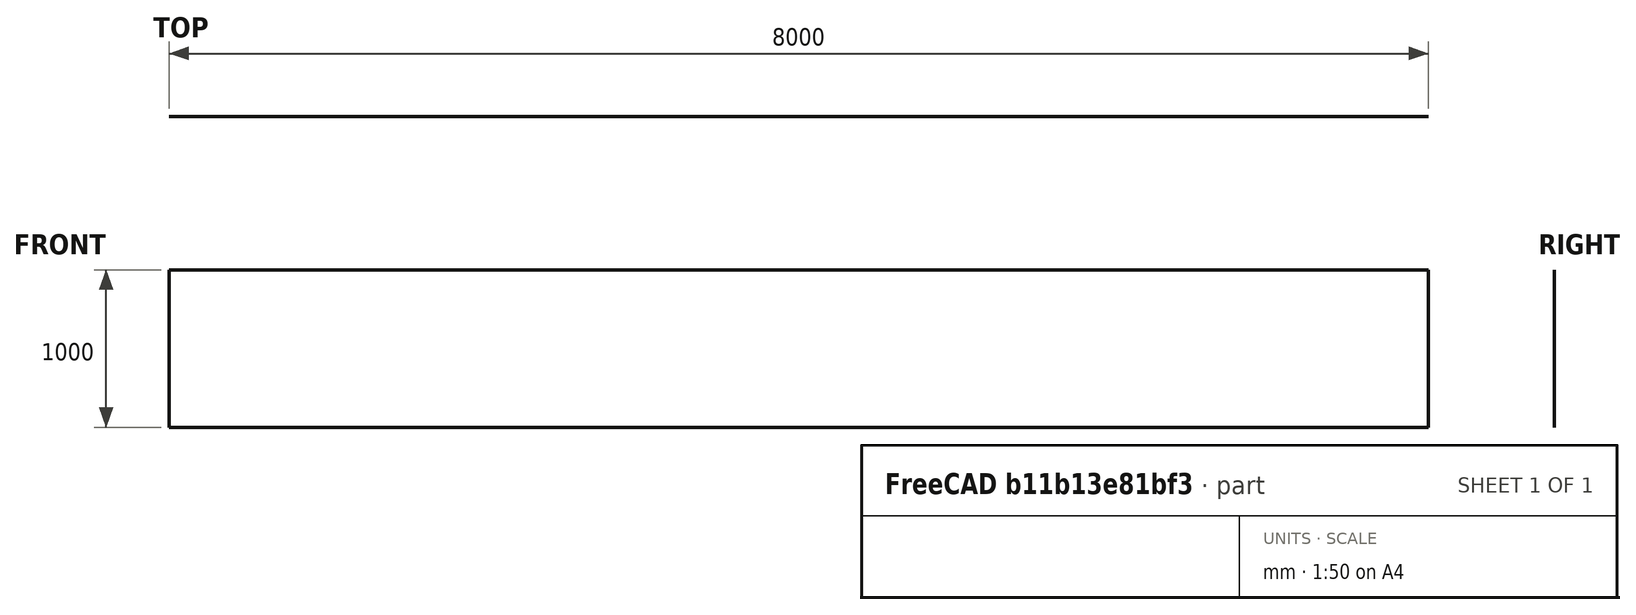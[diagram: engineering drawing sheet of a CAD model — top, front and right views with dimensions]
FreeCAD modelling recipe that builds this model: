
FCSTD DOCUMENT  (FreeCAD 0.17R13142 (Git))
Label: FemCalculixCantilever2D
License: CC-BY 3.0
LicenseURL: http://creativecommons.org/licenses/by/3.0/
objects: Fem::FemMeshObjectPython×2, Part::Plane×1, Fem::FemSolverObjectPython×1, Fem::ConstraintFixed×1, Fem::ConstraintForce×1, App::MaterialObjectPython×1, Fem::FeaturePython×1, Fem::FemResultObjectPython×1, Fem::FemAnalysis×1
note: 1 computed .brp shape members not serialized (recipe doc carries the construction recipe); baked Part::Feature solids carry a one-line shape summary decoded from their .brp

FEATURE [Part::Plane] Plane
  AttacherType = Attacher::AttachEngine3D
  Length = 8000
  Placement = pos=(0,500,0) rot=(1,0,0;1.5708rad)
  Width = 1000
FEATURE [Fem::FemMeshObjectPython] FEMMeshGmsh  # FEM object (typed FeaturePython)
  Algorithm2D = 0
  Algorithm3D = 0
  CharacteristicLengthMax = 500
  CharacteristicLengthMin = 0
  CoherenceMesh = true
  ElementDimension = 0
  ElementOrder = 1
  GeometryTolerance = 1e-06
  GroupsOfNodes = false
  HighOrderOptimize = false
  OptimizeNetgen = false
  OptimizeStd = true
  Part = -> Plane
  RecombineAll = false
FEATURE [Fem::FemSolverObjectPython] CalculiXccxTools  # FEM object (typed FeaturePython)
  AnalysisType = 0
  BeamShellResultOutput3D = false
  EigenmodeHighLimit = 0
  EigenmodeLowLimit = 0
  EigenmodesCount = 15
  GeometricalNonlinearity = 0
  IterationsControlParameterCutb = 0.25,0.5,0.75,0.85,,,1.5,
  IterationsControlParameterIter = 4,8,9,200,10,400,,200,,
  IterationsControlParameterTimeUse = false
  IterationsThermoMechMaximum = 2000
  IterationsUserDefinedIncrementations = false
  IterationsUserDefinedTimeStepLength = false
  MaterialNonlinearity = 0
  MatrixSolverType = 0
  SplitInputWriter = false
  ThermoMechSteadyState = true
  TimeEnd = 1
  TimeInitialStep = 1
FEATURE [Fem::ConstraintFixed] FemConstraintFixed
  NormalDirection = (0,0,1)
  Normals = (4) [(0,0,1),(0,0,1),(0,0,1),(0,0,1)]
  Points = (4) [(0,500,0),(0,500,333.333),(0,500,666.667),(0,500,1000)]
  References = -> [Plane]
  Scale = 33
FEATURE [Fem::ConstraintForce] FemConstraintForce
  Direction = -> Plane [Edge3]
  DirectionVector = (0,0,-1)
  Force = 9000000
  NormalDirection = (0,0,1)
  Points = (4) [(8000,500,0),(8000,500,333.333),(8000,500,666.667),(8000,500,1000)]
  References = -> [Plane]
  Reversed = true
  Scale = 33
FEATURE [App::MaterialObjectPython] SolidMaterial  # material (typed FeaturePython)
  Category = 0
  Material = Density=7900.0 kg/m^3,Description=Standard steel material for CalculiX sample calculations,Father=Metal,Name=CalculiX-Steel,PoissonRatio=0.3,+4 more (map truncated)
FEATURE [Fem::FeaturePython] ElementGeometry2D  # FEM object (typed FeaturePython)
  Thickness = 1000
FEATURE [Fem::FemMeshObjectPython] Result_mesh  # FEM object (typed FeaturePython)
FEATURE [Fem::FemResultObjectPython] CalculiX_static_results  # FEM object (typed FeaturePython)
  DisplacementLengths = [0,0,88.7247,88.7245,0,0,0,1.17213,2.87021,5.321,8.55561,12.5407,17.2233,22.544,28.4407,34.8502,41.7091,48.9533,56.519,64.3418,72.3578,80.5029,0.536992,1.86966,3.92405,6.76804,10.3869,14.7327,19.7474,25.3698,31.537,38.1854,45.2512,52.6705,+143 more]
  DisplacementVectors = (177) [(0,0,0),(0,0,0),(-8.21231,-3.06688e-11,-88.3438),(8.21213,-2.39886e-11,-88.3436),(0,0,0),(0,0,0),(0,0,0),(-0.977523,-6.0172e-13,-0.646785),+169 more]
  Eigenmode = 0
  EigenmodeFrequency = 0
  MaxShear = [201.8,202.026,5.41337,5.30679,18.419,92.3785,93.2253,204.695,190.185,176.731,163.226,149.723,136.223,122.723,109.223,95.7227,82.2227,68.7218,55.2082,41.6716,28.0358,14.2573,206.941,196.492,183.393,169.975,156.475,142.974,129.475,115.975,+147 more]
  Mesh = -> Result_mesh
  NodeNumbers = [1,2,3,4,5,6,7,8,9,10,11,12,13,14,15,16,17,18,19,20,21,22,23,24,25,26,27,28,29,30,31,32,33,34,35,36,37,38,39,40,41,42,43,44,45,46,47,48,49,50,51,52,53,54,55,56,57,58,59,60,61,62,63,64,65,66,67,68,69,+108 more]
  PrincipalMax = [-32.3491,436.468,7.21767,3.72084,16.8368,-17.785,205.07,11.7936,2.35037,2.42748,2.44818,2.44675,2.44643,2.44645,2.44645,2.44641,2.44641,2.4466,2.43641,2.39663,2.28289,0.841679,-2.58118,2.08778,2.41055,2.45398,2.45172,2.4503,2.4502,2.4502,+147 more]
  PrincipalMed = [-103.468,99.6002,-0.411076,0.470869,-0.747008,-66.2443,67.3588,-2.14053,-2.01228,-2.41488,-2.44752,-2.44633,-2.44639,-2.44645,-2.44645,-2.44643,-2.44645,-2.44652,-2.43851,-2.39408,-2.28825,-1.77715,-17.5975,-2.30258,-2.27694,-2.4311,+151 more]
  PrincipalMin = [-435.949,32.4159,-3.60908,-6.89275,-20.0011,-202.542,18.6194,-397.597,-378.019,-351.035,-324.004,-296.999,-269.999,-242.999,-215.999,-188.999,-161.999,-134.997,-107.98,-80.9465,-53.7887,-27.673,-416.464,-390.896,-364.375,-337.497,-310.499,+150 more]
  ResultType = Fem::FemResultMechanical
  Stats = [-8.21231,-0.0238928,8.21213,-3.06688e-11,-1.29243e-11,5.70655e-14,-88.3438,-34.1051,0.0121269,0,34.3914,88.7247,9.41896,131.776,406.592,-32.3491,68.0175,436.468,-103.468,-0.275923,99.6002,-435.949,-68.9793,32.4159,5.30679,68.4984,207.147,0,+11 more]
  StrainVectors = (177) [(-0.00188192,0.000552389,0.000240456),(0.00188983,-0.000554245,-0.000252753),(-2.69098e-05,3.95158e-06,2.90487e-05),+174 more]
  StressValues = [373.158,375.001,9.6344,9.41896,31.9135,165.922,167.487,402.604,378.207,351.066,324.032,297.029,270.032,243.036,216.041,189.046,162.054,135.064,108.061,81.054,53.9315,27.2996,406.583,390.807,364.464,337.535,310.529,283.53,256.534,229.538,+147 more]
  StressVectors = (177) [(-435.949,-42.7141,-93.1033),(436.468,41.6567,90.3594),(-3.60908,1.37622,5.43037),(3.72084,-1.33895,-5.08293),(-0.747008,-0.867611,-2.29663),+172 more]
  Time = 0
FEATURE [Fem::FemAnalysis] Analysis
  Group = -> [CalculiXccxTools,FemConstraintFixed,FemConstraintForce,SolidMaterial,ElementGeometry2D,FEMMeshGmsh,CalculiX_static_results]
